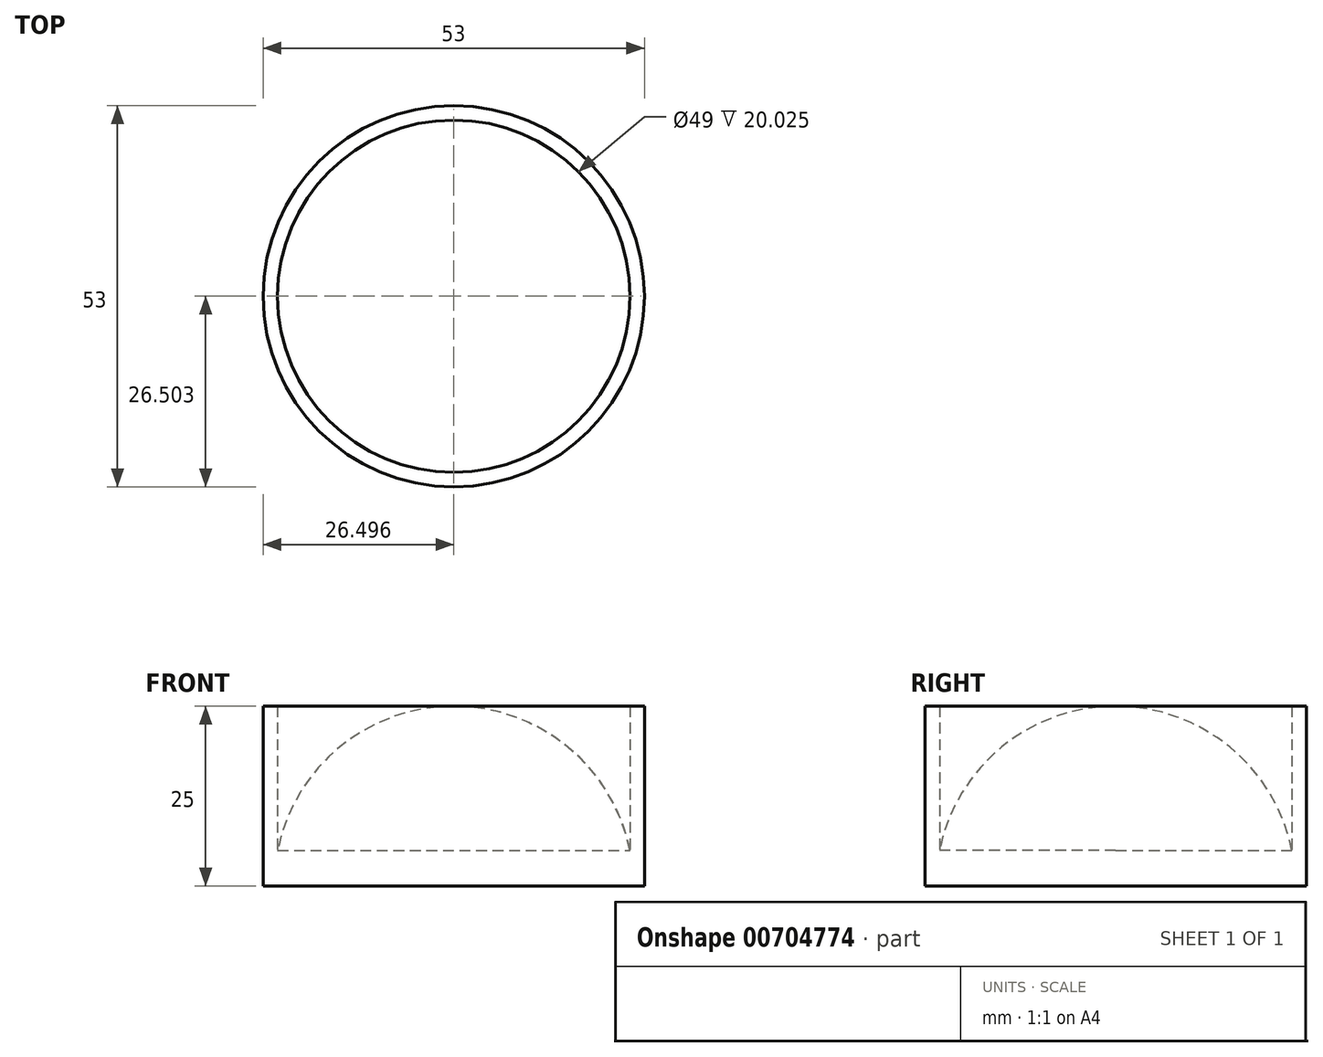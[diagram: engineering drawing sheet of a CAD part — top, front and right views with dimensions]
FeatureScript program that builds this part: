
annotation { "Feature Type Name" : "Feature", "Feature Type Description" : "" }
export const myFeature = defineFeature(function(context is Context, id is Id, definition is map)
    precondition{}
    {
        {
            var Q0;
            Q0=qCreatedBy(makeId("Top.planeOp"),FACE);
            var sketch = newSketch(context, id + "F0", { "sketchPlane" : qUnion([Q0])});
            skCircle(sketch, "E0", {"center": v(-7.37, 10.74) * mm, "radius": 25 * mm});
            skSolve(sketch);
        }
        {
            var Q0;
            Q0 = qSketchRegion(id + "F0", true);
            extrude(context, id + "F1", {"entities" : qUnion([Q0]), "depth" : 25 * mm, "offsetDistance" : 25 * mm});
        }
        {
            var Q0;
            Q0=makeQuery(id+"F1.opExtrude","CAP_EDGE",EDGE,{"disambiguationData":[OSD([sQuery(id+"F0.wireOp",EDGE,"E0")])],"isStart":false});
            fillet(context, id + "F2", {"entities" : qUnion([Q0]), "radius" : 25 * mm, "tangentPropagation" : true, "allowEdgeOverflow" : false});
        }
        {
            var Q0;
            Q0=qCreatedBy(makeId("Top.planeOp"),FACE);
            var sketch = newSketch(context, id + "F3", { "sketchPlane" : qUnion([Q0])});
            skCircle(sketch, "E1", {"center": v(-7.37, 10.74) * mm, "radius": 24.5 * mm});
            skCircle(sketch, "E2.0", {"center": v(-7.37, 10.74) * mm, "radius": 26.5 * mm});
            skSolve(sketch);
        }
        {
            var Q0;
            Q0=makeQuery(id+"F3.imprint","IMPRINT",FACE,{"disambiguationData":[TD([[makeQuery(id+"F3.imprint","IMPRINT",EDGE,{"derivedFrom":sQuery(id+"F3.wireOp",EDGE,"E1")}),-1.0]])]});
            extrude(context, id + "F4", {"entities" : qUnion([Q0]), "operationType" : NewBodyOperationType.ADD, "depth" : 25 * mm, "offsetDistance" : 25 * mm});
        }
    });
